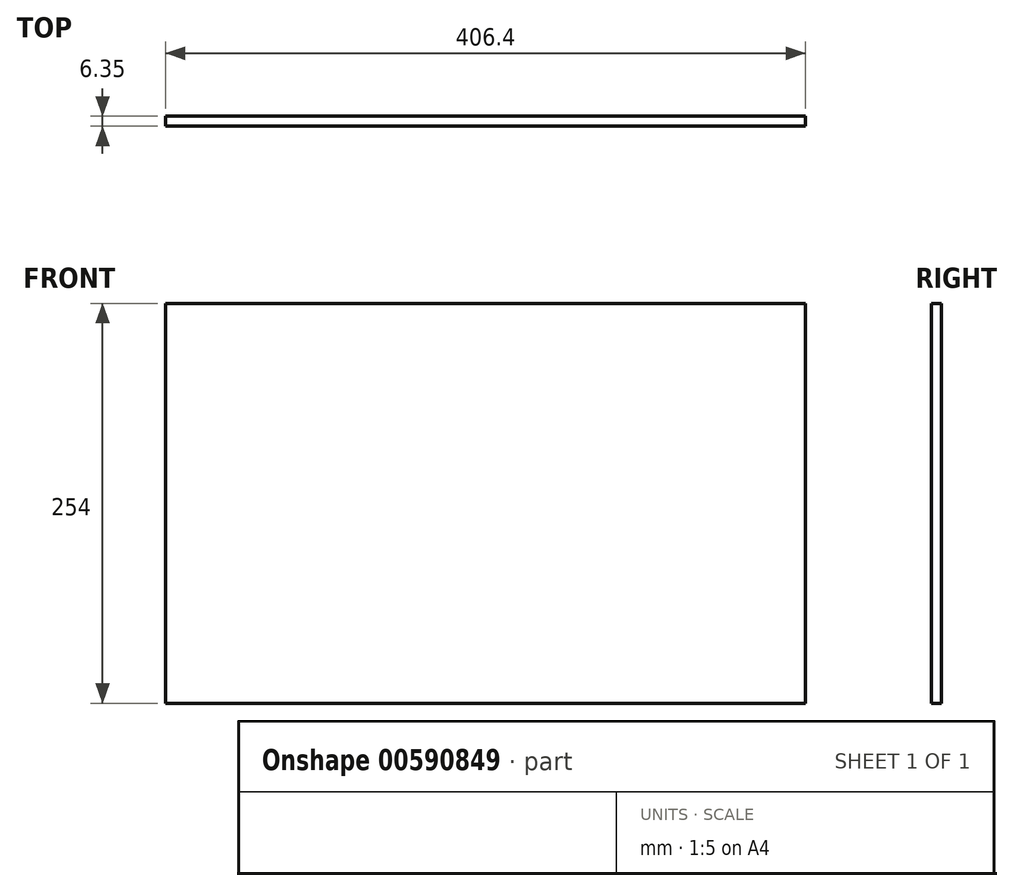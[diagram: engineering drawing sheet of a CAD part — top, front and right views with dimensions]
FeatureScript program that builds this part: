
annotation { "Feature Type Name" : "Feature", "Feature Type Description" : "" }
export const myFeature = defineFeature(function(context is Context, id is Id, definition is map)
    precondition{}
    {
        {
            var Q0;
            Q0=qCreatedBy(makeId("Front.planeOp"),FACE);
            var sketch = newSketch(context, id + "F0", { "sketchPlane" : qUnion([Q0])});
            skLineSegment(sketch, "E0.bottom", {"start": v(-163.47, 107.63) * mm, "end": v(242.93, 107.63) * mm});
            skLineSegment(sketch, "E0.top", {"start": v(-163.47, -146.37) * mm, "end": v(242.93, -146.37) * mm});
            skLineSegment(sketch, "E0.left", {"start": v(-163.47, 107.63) * mm, "end": v(-163.47, -146.37) * mm});
            skLineSegment(sketch, "E0.right", {"start": v(242.93, 107.63) * mm, "end": v(242.93, -146.37) * mm});
            skSolve(sketch);
        }
        {
            var Q0;
            Q0=makeQuery(id+"F0.imprint","IMPRINT",FACE,{"disambiguationData":[TD([[makeQuery(id+"F0.imprint","IMPRINT",EDGE,{"derivedFrom":sQuery(id+"F0.wireOp",EDGE,"E0.bottom")}),-1.0]])]});
            extrude(context, id + "F1", {"entities" : qUnion([Q0]), "depth" : 6.35 * mm, "offsetDistance" : 25.4 * mm});
        }
    });
